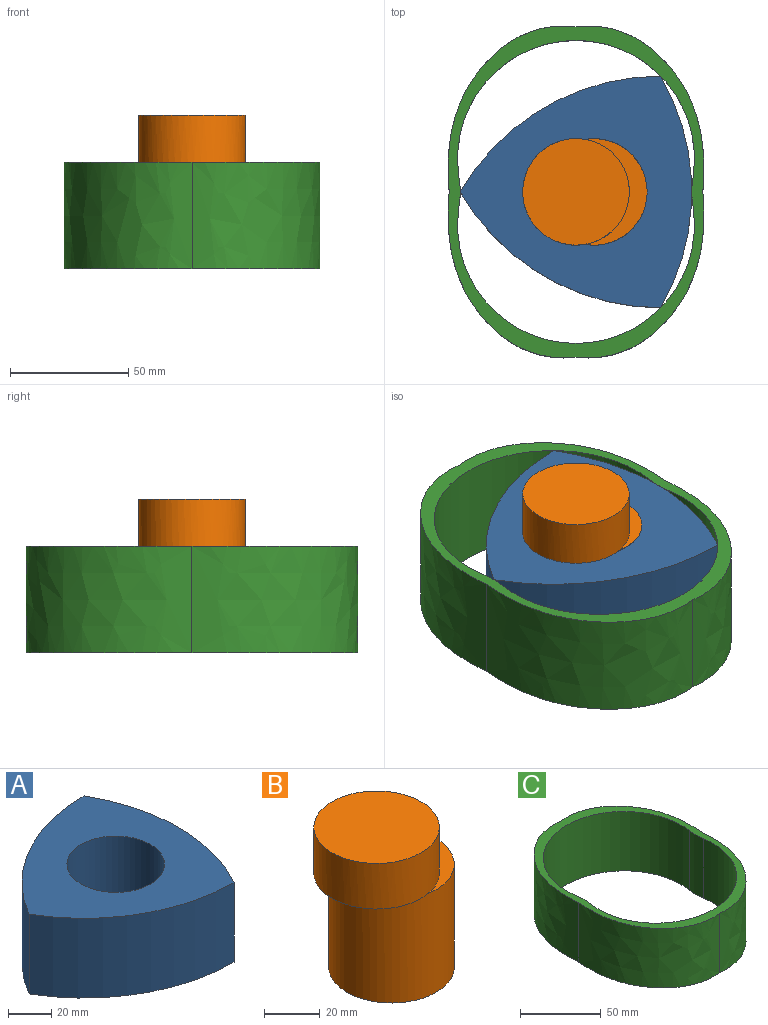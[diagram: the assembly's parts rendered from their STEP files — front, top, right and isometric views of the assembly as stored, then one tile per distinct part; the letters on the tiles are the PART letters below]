
ASSEMBLY  parts=3 mates=2
PART A: 6 faces, bbox 97.8x97.8x45 mm
  f0: cylinder r=97.79mm len=97.79mm, axis (0,0,1), area 4608.3mm2, adj f1,f2,f4,f5
  f1: cylinder r=97.79mm len=84.69mm, axis (0,0,1), area 4608.3mm2, adj f0,f2,f4,f5
  f2: cylinder r=97.79mm len=84.69mm, axis (0,0,1), area 4608.3mm2, adj f0,f1,f4,f5
  f3: cylinder r=22.5mm len=45mm, axis (0,0,1), area 6361.7mm2, adj f4,f5
  f4: plane 97.79x97.79mm, normal (0,0,-1), area 5149.4mm2, adj f0,f1,f2,f3
  f5: plane 97.79x97.79mm, normal (0,0,1), area 5149.4mm2, adj f0,f1,f2,f3
PART B: 6 faces, bbox 52.6x45x65 mm
  f0: cylinder r=22.5mm len=45mm, axis (0,0,1), area 6361.7mm2, adj f1,f2,f3
  f1: plane 45x45mm, normal (0,0,-1), area 1590.4mm2, adj f0
  f2: plane 45x26.28mm, normal (0,0,1), area 338.2mm2, adj f0,f4
  f3: plane 45x26.28mm, normal (0,0,-1), area 338.2mm2, adj f0,f4
  f4: cylinder r=22.5mm len=45mm, axis (0,0,-1), area 2827.4mm2, adj f2,f3,f5
  f5: plane 45x45mm, normal (0,0,1), area 1590.4mm2, adj f4
PART C: 10 faces, bbox 110.8x142.7x45 mm
  f0: extruded ~70.02x54.03mm, area 4553.2mm2, adj f1,f5,f6,f7
  f1: extruded ~70.02x54.03mm, area 4553.2mm2, adj f0,f2,f6,f7
  f2: extruded ~70.02x54.03mm, area 4553.2mm2, adj f1,f5,f6,f7
  f3: cylinder r=50mm len=100mm, axis (0,0,-1), area 7769.9mm2, adj f6,f7,f8,f9
  f4: cylinder r=50mm len=100mm, axis (0,0,-1), area 7769.9mm2, adj f6,f7,f8,f9
  f5: extruded ~70.02x54.03mm, area 4553.2mm2, adj f0,f2,f6,f7
  f6: plane 142.71x110.82mm, normal (0,0,1), area 2045.3mm2, adj f0,f1,f2,f3,f4,f5,f8,f9
  f7: plane 142.71x110.82mm, normal (0,0,-1), area 2045.3mm2, adj f0,f1,f2,f3,f4,f5,f8,f9
  f8: cylinder r=40mm len=45mm, axis (0,0,-1), area 561.1mm2, adj f3,f4,f6,f7
  f9: cylinder r=40mm len=45mm, axis (0,0,-1), area 561.1mm2, adj f3,f4,f6,f7
PLACE A t=(-24.49,10.48,-3.38)mm
PLACE B t=(-24.49,10.48,-3.38)mm
PLACE C t=(-24.49,10.48,-3.38)mm fixed
MATE revolute A.f3 <-> B.f0  axis (0,0,-1) through (-16.94,-0.38,-3.38)mm
MATE revolute B.f4 <-> C.f6  axis (0,0,-1) through (-24.49,-0.38,41.62)mm
